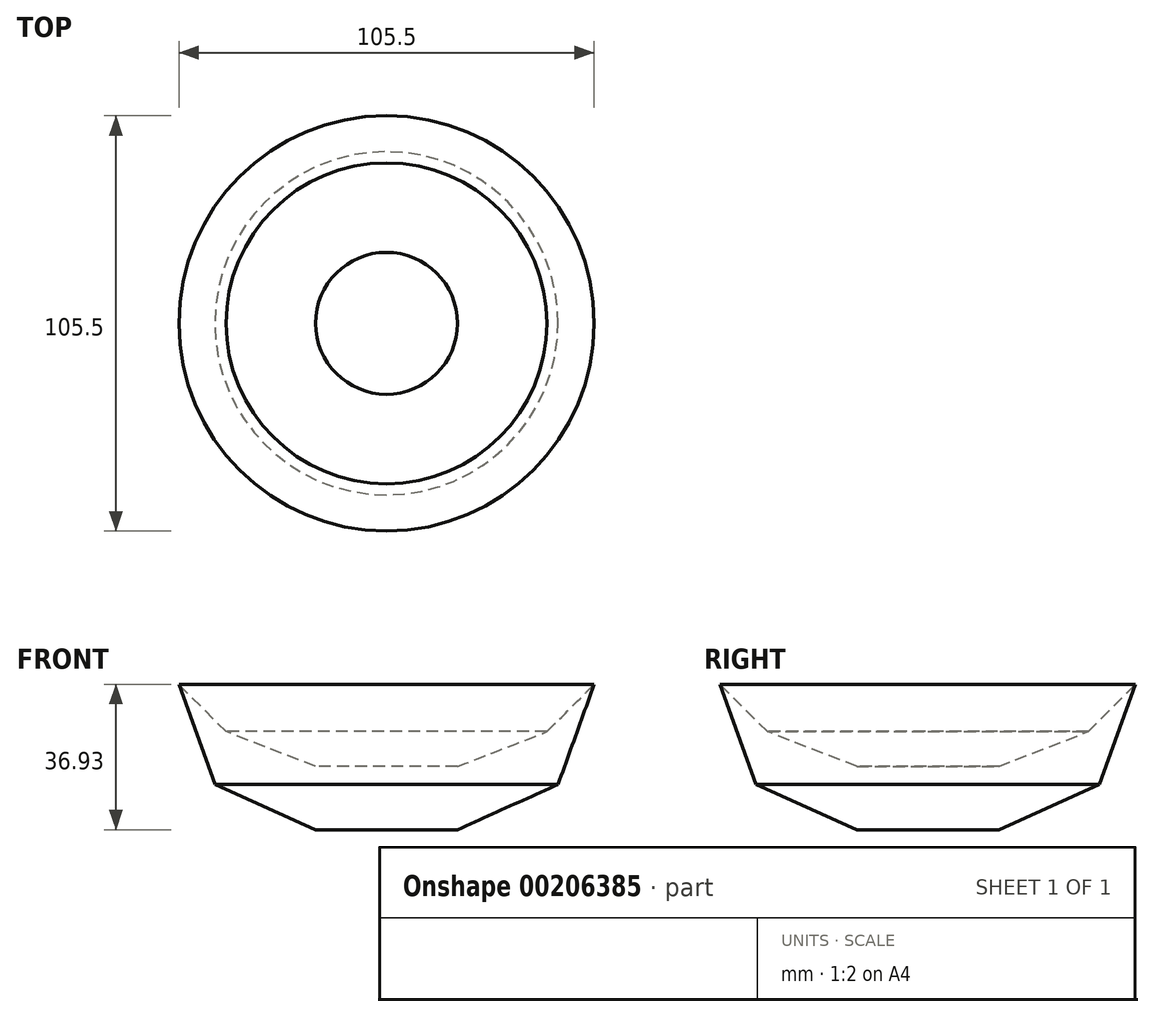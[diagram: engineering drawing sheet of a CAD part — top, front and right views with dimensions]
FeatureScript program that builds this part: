
annotation { "Feature Type Name" : "Feature", "Feature Type Description" : "" }
export const myFeature = defineFeature(function(context is Context, id is Id, definition is map)
    precondition{}
    {
        {
            var Q0;
            Q0=qCreatedBy(makeId("Front.planeOp"),FACE);
            var sketch = newSketch(context, id + "F0", { "sketchPlane" : qUnion([Q0])});
            skLineSegment(sketch, "E0", {"start": v(-52.75, 25.4) * mm, "end": v(-40.76, 13.4) * mm});
            skLineSegment(sketch, "E1", {"start": v(-40.76, 13.4) * mm, "end": v(-18.03, 4.56) * mm});
            skLineSegment(sketch, "E2", {"start": v(-18.03, 4.56) * mm, "end": v(0, 4.56) * mm});
            skLineSegment(sketch, "E3", {"start": v(0, 4.56) * mm, "end": v(0, -11.54) * mm});
            skLineSegment(sketch, "E4", {"start": v(0, -11.54) * mm, "end": v(-18.03, -11.54) * mm});
            skLineSegment(sketch, "E5", {"start": v(-18.03, -11.54) * mm, "end": v(-43.6, 0) * mm});
            skLineSegment(sketch, "E6", {"start": v(-43.6, 0) * mm, "end": v(-52.75, 25.4) * mm});
            skSolve(sketch);
        }
        {
            var Q0;
            Q0=makeQuery(id+"F0.imprint","IMPRINT",FACE,{"disambiguationData":[TD([[makeQuery(id+"F0.imprint","IMPRINT",EDGE,{"derivedFrom":sQuery(id+"F0.wireOp",EDGE,"E0")}),-1.0]])]});
            var Q1;
            Q1=sQuery(id+"F0.wireOp",EDGE,"E3");
            revolve(context, id + "F1", {"entities" : qUnion([Q0]), "axis" : qUnion([Q1]), "revolveType" : RevolveType.FULL});
        }
    });
